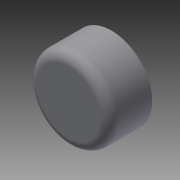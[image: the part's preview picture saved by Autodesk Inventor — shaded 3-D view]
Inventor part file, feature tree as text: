
AUTODESK INVENTOR PART (.ipt)
format: ipt  version: 2014 SP2 (Build 180246200, 246)  size: 134,656 bytes
history: native  units: mm
features: extrude x4, sketch x4, chamfer x2, fillet x1
ambient origin geometry x8: Origin, YZ Plane, XZ Plane, XY Plane, X Axis, Y Axis, Z Axis, Center Point
bodies: Solid1 (feature_tree)
feature tree (11):
  extrude  "Extrusion1"  Depth=8.0mm
  chamfer  "Chamfer1"  Distance=8.0mm
  extrude  "Extrusion2"  Depth=1.0mm TaperAngle=0.0deg
  fillet  "Fillet1"  Radius=2.0mm
  extrude  "Extrusion3"  Depth=1.0mm TaperAngle=0.0deg
  extrude  "Extrusion4"  Depth=1.0mm TaperAngle=0.0deg
  chamfer  "Chamfer2"  Distance=2.0mm Angle=45.0deg
  sketch  "Sketch1"  dims[d0=3.0mm d1=17.0mm d2=8.0mm d3=0.0mm]
  sketch  "Sketch2"  dims[d4=0.5mm d5=7.0mm d6=45.0deg d7=1.0mm d8=0.0mm d9=2.0mm]
  sketch  "Sketch3"  dims[d10=7.0mm d11=1.0mm d12=0.0mm]
  sketch  "Sketch4"  dims[d13=4.0mm d14=1.0mm d15=0.0mm d16=0.5mm d17=2.0mm d18=45.0deg]
